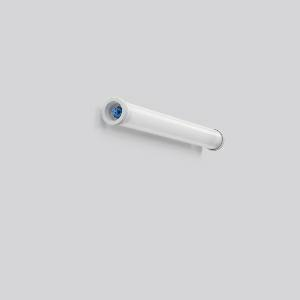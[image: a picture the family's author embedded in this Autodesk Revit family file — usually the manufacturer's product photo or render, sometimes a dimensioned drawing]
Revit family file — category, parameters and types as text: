
# Revit family: planox_tube_601070_002_1_c6ff
name_source: partatom
category: Lighting Fixtures
units: mm (PartAtom-declared; Revit-internal decimal feet)

## family parameters
Cut with Voids When Loaded = No
Host = Face
Light Source = No
Part Type = Normal
Room Calculation Point = No
Round Connector Dimension = Use Diameter
Shared = No

## types (1)
- PLANOX TUBE (1 x LED Modul 840, 3500 lm, 4000)
    Apparent Load = 31 VA
    CIE Flux Codes = 41 70 89 89 100
    Color Rendering = 80
    Color Temperature = 4000
    Default Elevation = 1800 mm
    Description = Series: PLANOX TUBE
Robust protective tube luminaire for tough requirements. Rack made of sheet steel, white powder coated. End caps made of plastic (polyamide) grey. Diffuser made of plastic (polycarbonate), opal, shockproof. Symmetrical light distribution. Homogeneous light distribution. With accessories for wall, ceiling or pendant mounting. Driver integrated. Easy installation with the Plug+Play Wieland RST CLASSIC plug-in system. Luminaire with integrated through-wiring for series connection of further luminaires by two Wieland RST Classic plug connectors (plug and socket). Accessories for electrical connection must be ordered separately. Mounting set must be ordered separately. Luminaire with limited surface temperature in accordance with EN 60598-2-24 for use in environments in which a deposit of conductive dust on the luminaire can be expected. Qualified for use in the food and drink industry. Suitable for lighting in public car parks and public off-street parking spaces according to DIN 67528. Environmentally friendly and resource-saving due to replaceable components. 
Colour: white
Diameter: 78 mm
Length: 722 mm
Lamp: LED
Socket: without socket
Colour temperature: 4000K
Colour rendering index (CRI): 83
System power: 31 W
Rated luminous flux: 3500 lm
Luminous efficiency: 113 lm/W
Control gear: Regulated power supply
Protection class: I
Type of protection: IP 67
    Height = 0 mm  [stored 0 ft]
    Lamp = 1 x LED Modul 840
    Lamp Light Flux = 3500 lm
    Lamp count = 1
    Length = 722 mm
    Lifetime = 50000 h
    Luminous efficacy = 113 lm/W
    Manufacturer = RZB
    ModVariant = No
    Model = 601070.002.1
    Mounting Place = Ceiling
    Mounting Type = Surface mounted
    Number of Poles = 1
    OnlyDefault = Yes
    Power Factor = 1
    Product Name = PLANOX TUBE
    Product group = Surface mounted luminaires for moist/humid enviroments
    ProductGroupID = 308
    Protection Class = Protection class I
    Protection Degree = Degree of protection
    RLX_Detail_Level = 1
    RLX_Emergency_Light_Flux = 0 lm
    RLX_Emergency_Type = 0
    RLX_Emergency_Type_DB = No
    RlxData = <blob elided: 31801 chars, md5=aef65fc2>
    Socket = socket
    Standby Power = 0 W
    System Light Flux = 3500 lm
    System Power = 31 W
    Type Comments = Product without accessories
    Type Image = 601070.002.jpg
    URL = http://relux.com
    VarID = ---
    Voltage = 0 V
    Weight = 0.00 kg
    Width = 0 mm  [stored 0 ft]

note: [stored X ft] marks values corroborated as IEEE doubles in the binary element streams (Revit-internal decimal feet)

## geometry (parser evidence)
native form markers: Blend x4, Sweep x12
no freeform markers — native parametric forms only
